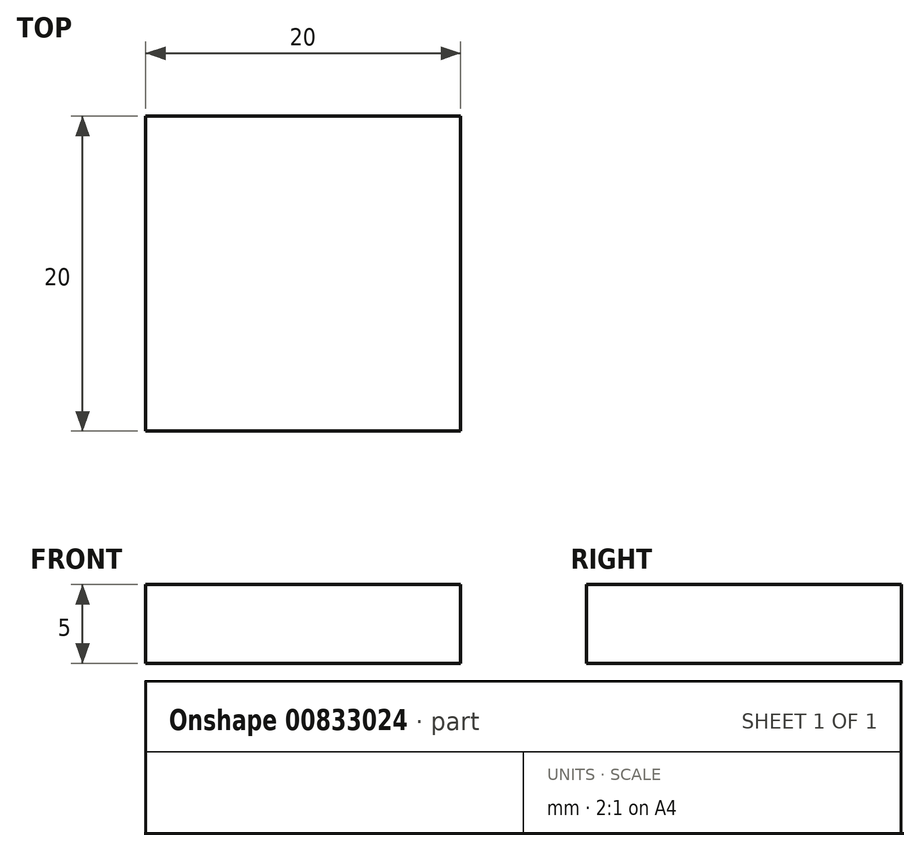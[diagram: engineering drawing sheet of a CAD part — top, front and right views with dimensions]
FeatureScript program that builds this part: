
annotation { "Feature Type Name" : "Feature", "Feature Type Description" : "" }
export const myFeature = defineFeature(function(context is Context, id is Id, definition is map)
    precondition{}
    {
        {
            var Q0;
            Q0=qCreatedBy(makeId("Front.planeOp"),FACE);
            var sketch = newSketch(context, id + "F0", { "sketchPlane" : qUnion([Q0])});
            skCircle(sketch, "E0", {"center": v(-21.6, 0) * mm, "radius": 7.5 * mm});
            skSolve(sketch);
        }
        {
            var Q0;
            Q0=qCreatedBy(makeId("Top.planeOp"),FACE);
            var sketch = newSketch(context, id + "F1", { "sketchPlane" : qUnion([Q0])});
            skArc(sketch, "E1", {"start": v(0, -37.38) * mm, "mid": v(37.38, 0) * mm, "end": v(0, 37.38) * mm});
            skSolve(sketch);
        }
        {
            var Q0;
            Q0=qCreatedBy(makeId("Top.planeOp"),FACE);
            var sketch = newSketch(context, id + "F2", { "sketchPlane" : qUnion([Q0])});
            skLineSegment(sketch, "E2.top", {"start": v(-20.04, 10) * mm, "end": v(-40.04, 10) * mm});
            skLineSegment(sketch, "E2.left", {"start": v(-20.04, 0) * mm, "end": v(-20.04, 10) * mm});
            skLineSegment(sketch, "E2.right", {"start": v(-40.04, 0) * mm, "end": v(-40.04, 10) * mm});
            skLineSegment(sketch, "E3.top", {"start": v(-20.04, -10) * mm, "end": v(-40.04, -10) * mm});
            skLineSegment(sketch, "E3.left", {"start": v(-20.04, 0) * mm, "end": v(-20.04, -10) * mm});
            skLineSegment(sketch, "E3.right", {"start": v(-40.04, 0) * mm, "end": v(-40.04, -10) * mm});
            skSolve(sketch);
        }
        {
            var Q0;
            Q0=makeQuery(id+"F2.imprint","IMPRINT",FACE,{"disambiguationData":[TD([[makeQuery(id+"F2.imprint","IMPRINT",EDGE,{"derivedFrom":sQuery(id+"F2.wireOp",EDGE,"E2.top")}),1.0]])]});
            extrude(context, id + "F3", {"entities" : qUnion([Q0]), "depth" : 5 * mm, "offsetDistance" : 25 * mm});
        }
    });
